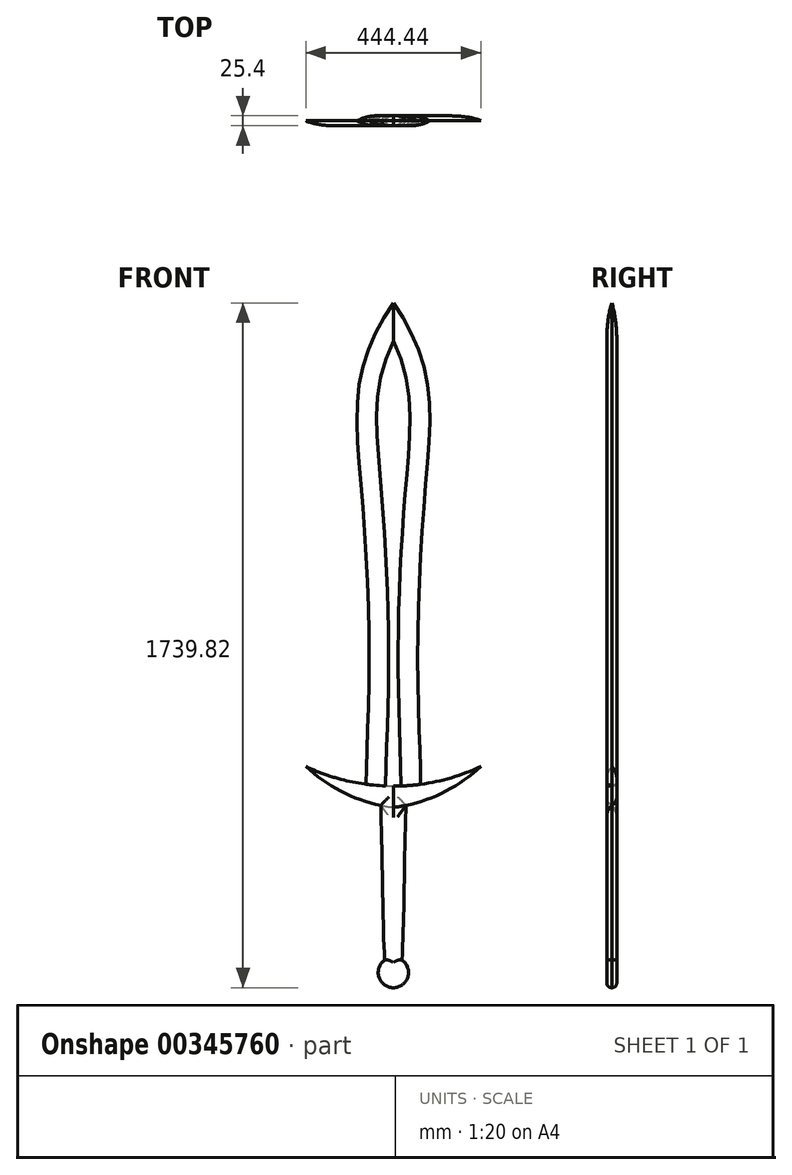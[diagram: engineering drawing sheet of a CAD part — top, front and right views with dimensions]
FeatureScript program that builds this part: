
annotation { "Feature Type Name" : "Feature", "Feature Type Description" : "" }
export const myFeature = defineFeature(function(context is Context, id is Id, definition is map)
    precondition{}
    {
        {
            var Q0;
            Q0=qCreatedBy(makeId("Front.planeOp"),FACE);
            var sketch = newSketch(context, id + "F0", { "sketchPlane" : qUnion([Q0])});
            skLineSegment(sketch, "E0", {"start": v(0, 836.26) * mm, "end": v(0, -840.14) * mm});
            skFitSpline(sketch, "E1", {"points": [v(0, 836.26) * mm, v(-85.7, 634.86) * mm, v(-80.11, 351.26) * mm, v(-61.73, -84.8) * mm, v(-69.32, -386.69) * mm], "startDerivative": vector(-583.16, -808.43) * mm, "endDerivative": vector(-5.13, -843.12) * mm});
            skArc(sketch, "E2", {"start": v(-222.22, -341.63) * mm, "mid": v(-113.84, -378.72) * mm, "end": v(0, -391.38) * mm});
            skArc(sketch, "E3", {"start": v(-222.22, -341.63) * mm, "mid": v(-119.4, -411.33) * mm, "end": v(0, -445.58) * mm});
            skFitSpline(sketch, "E4", {"points": [v(-31.83, -440.37) * mm, v(-29.25, -549) * mm, v(-26.9, -681.75) * mm, v(-21.72, -841.97) * mm], "startDerivative": vector(2.38, -327.28) * mm, "endDerivative": vector(22.91, -400.96) * mm});
            skFitSpline(sketch, "E5.MirrorCS", {"points": [v(0, 836.26) * mm, v(85.7, 634.86) * mm, v(80.11, 351.26) * mm, v(61.73, -84.8) * mm, v(69.32, -386.69) * mm], "startDerivative": vector(583.16, -808.43) * mm, "endDerivative": vector(5.13, -843.12) * mm});
            skArc(sketch, "E6.MirrorCS", {"start": v(222.22, -341.63) * mm, "mid": v(113.84, -378.72) * mm, "end": v(0, -391.38) * mm});
            skArc(sketch, "E7.MirrorCS", {"start": v(222.22, -341.63) * mm, "mid": v(119.4, -411.33) * mm, "end": v(0, -445.58) * mm});
            skFitSpline(sketch, "E8.MirrorCS", {"points": [v(31.83, -440.37) * mm, v(29.25, -549) * mm, v(26.9, -681.75) * mm, v(21.72, -841.97) * mm], "startDerivative": vector(-2.38, -327.28) * mm, "endDerivative": vector(-22.91, -400.96) * mm});
            skCircle(sketch, "E9", {"center": v(0, -865.08) * mm, "radius": 38.48 * mm});
            skSolve(sketch);
        }
        {
            var Q0;
            {var subQ0=sQuery(id+"F0.wireOp",EDGE,"E1");Q0=makeQuery(id+"F0.imprint","IMPRINT",FACE,{"disambiguationData":[TD([[makeQuery(id+"F0.imprint","IMPRINT",EDGE,{"derivedFrom":subQ0}),1.0]])]});}
            var Q1;
            {var subQ0=sQuery(id+"F0.wireOp",EDGE,"E5.MirrorCS");Q1=makeQuery(id+"F0.imprint","IMPRINT",FACE,{"disambiguationData":[TD([[makeQuery(id+"F0.imprint","IMPRINT",EDGE,{"derivedFrom":subQ0}),-1.0]])]});}
            var Q2;
            {var subQ0=sQuery(id+"F0.wireOp",EDGE,"E2");var subQ1=makeQuery(id+"F0.imprint","INTERSECT",VERTEX,{"derivedFrom":[sQuery(id+"F0.wireOp",EDGE,"E1"),subQ0]});Q2=makeQuery(id+"F0.imprint","IMPRINT",FACE,{"disambiguationData":[TD([[makeQuery(id+"F0.imprint","IMPRINT",EDGE,{"disambiguationData":[TD([[subQ1,1.0]])],"derivedFrom":subQ0}),-1.0]])]});}
            var Q3;
            {var subQ1=sQuery(id+"F0.wireOp",EDGE,"E6.MirrorCS");var subQ7=makeQuery(id+"F0.imprint","INTERSECT",VERTEX,{"derivedFrom":[sQuery(id+"F0.wireOp",EDGE,"E5.MirrorCS"),subQ1]});Q3=makeQuery(id+"F0.imprint","IMPRINT",FACE,{"disambiguationData":[TD([[makeQuery(id+"F0.imprint","IMPRINT",EDGE,{"disambiguationData":[TD([[subQ7,1.0]])],"derivedFrom":subQ1}),1.0]])]});}
            var Q4;
            {var subQ0=sQuery(id+"F0.wireOp",EDGE,"E7.MirrorCS");var subQ5=sQuery(id+"F0.wireOp",EDGE,"E8.MirrorCS");var subQ6=makeQuery(id+"F0.imprint","INTERSECT",VERTEX,{"derivedFrom":[subQ0,subQ5]});Q4=makeQuery(id+"F0.imprint","IMPRINT",FACE,{"disambiguationData":[TD([[makeQuery(id+"F0.imprint","IMPRINT",EDGE,{"disambiguationData":[TD([[subQ6,-1.0]])],"derivedFrom":subQ5}),-1.0]])]});}
            var Q5;
            {var subQ0=sQuery(id+"F0.wireOp",EDGE,"E3");var subQ5=sQuery(id+"F0.wireOp",EDGE,"E4");var subQ6=makeQuery(id+"F0.imprint","INTERSECT",VERTEX,{"derivedFrom":[subQ0,subQ5]});Q5=makeQuery(id+"F0.imprint","IMPRINT",FACE,{"disambiguationData":[TD([[makeQuery(id+"F0.imprint","IMPRINT",EDGE,{"disambiguationData":[TD([[subQ6,-1.0]])],"derivedFrom":subQ5}),1.0]])]});}
            var Q6;
            {var subQ0=sQuery(id+"F0.wireOp",EDGE,"E9");var subQ1=makeQuery(id+"F0.imprint","INTERSECT",VERTEX,{"derivedFrom":[sQuery(id+"F0.wireOp",EDGE,"E8.MirrorCS"),subQ0]});Q6=makeQuery(id+"F0.imprint","IMPRINT",FACE,{"disambiguationData":[TD([[makeQuery(id+"F0.imprint","IMPRINT",EDGE,{"disambiguationData":[TD([[subQ1,-1.0]])],"derivedFrom":subQ0}),1.0]])]});}
            extrude(context, id + "F1", {"entities" : qUnion([Q0, Q1, Q2, Q3, Q4, Q5, Q6]), "depth" : 12.7 * mm});
        }
        {
            var Q0;
            Q0=makeQuery(id+"F1.opExtrude","CAP_EDGE",EDGE,{"disambiguationData":[OSD([sQuery(id+"F0.wireOp",EDGE,"E1")])],"isStart":false});
            var Q1;
            Q1=makeQuery(id+"F1.opExtrude","CAP_EDGE",EDGE,{"disambiguationData":[OSD([sQuery(id+"F0.wireOp",EDGE,"E5.MirrorCS")])],"isStart":false});
            fillet(context, id + "F2", {"entities" : qUnion([Q0, Q1]), "radius" : 104.25 * mm, "tangentPropagation" : true, "allowEdgeOverflow" : false});
        }
        {
            var Q0;
            Q0=makeQuery(id+"F1.opExtrude","CAP_EDGE",EDGE,{"disambiguationData":[OSD([sQuery(id+"F0.wireOp",EDGE,"E4")])],"isStart":false});
            var Q1;
            Q1=makeQuery(id+"F1.opExtrude","CAP_EDGE",EDGE,{"disambiguationData":[OSD([sQuery(id+"F0.wireOp",EDGE,"E8.MirrorCS")])],"isStart":false});
            fillet(context, id + "F3", {"entities" : qUnion([Q0, Q1]), "radius" : 23.3 * mm, "tangentPropagation" : true, "allowEdgeOverflow" : false});
        }
        {
            var Q0;
            Q0=makeQuery(id+"F1.opExtrude","CAP_EDGE",EDGE,{"disambiguationData":[OSD([sQuery(id+"F0.wireOp",EDGE,"E9")])],"isStart":false});
            fillet(context, id + "F4", {"entities" : qUnion([Q0]), "radius" : 12.26 * mm, "tangentPropagation" : true, "allowEdgeOverflow" : false});
        }
        {
            var Q0;
            Q0=makeQuery(id+"F1.opExtrude","CAP_EDGE",EDGE,{"disambiguationData":[OSD([sQuery(id+"F0.wireOp",EDGE,"E3")])],"isStart":false});
            var Q1;
            Q1=makeQuery(id+"F1.opExtrude","CAP_EDGE",EDGE,{"disambiguationData":[OSD([sQuery(id+"F0.wireOp",EDGE,"E7.MirrorCS")])],"isStart":false});
            fillet(context, id + "F5", {"entities" : qUnion([Q0, Q1]), "radius" : 30.66 * mm, "tangentPropagation" : true, "allowEdgeOverflow" : false});
        }
        {
            var Q0;
            Q0=makeQuery(id+"F1.opExtrude","CAP_FACE",FACE,{"disambiguationData":[OSD([sQuery(id+"F0.wireOp",EDGE,"E1"),sQuery(id+"F0.wireOp",EDGE,"E2"),sQuery(id+"F0.wireOp",EDGE,"E3"),sQuery(id+"F0.wireOp",EDGE,"E4"),sQuery(id+"F0.wireOp",EDGE,"E5.MirrorCS"),sQuery(id+"F0.wireOp",EDGE,"E6.MirrorCS"),sQuery(id+"F0.wireOp",EDGE,"E7.MirrorCS"),sQuery(id+"F0.wireOp",EDGE,"E8.MirrorCS"),sQuery(id+"F0.wireOp",EDGE,"E9")])],"isStart":true});
            var sketch = newSketch(context, id + "F6", { "sketchPlane" : qUnion([Q0])});
            skLineSegment(sketch, "E10", {"start": v(0, 0) * mm, "end": v(0, 120.77) * mm});
            skSolve(sketch);
        }
        {
            var Q0;
            Q0=makeQuery(id+"F1.opExtrude","SWEPT_BODY",BODY,{"disambiguationData":[OSD([sQuery(id+"F0.wireOp",EDGE,"E1"),sQuery(id+"F0.wireOp",EDGE,"E2"),sQuery(id+"F0.wireOp",EDGE,"E3"),sQuery(id+"F0.wireOp",EDGE,"E4"),sQuery(id+"F0.wireOp",EDGE,"E5.MirrorCS"),sQuery(id+"F0.wireOp",EDGE,"E6.MirrorCS"),sQuery(id+"F0.wireOp",EDGE,"E7.MirrorCS"),sQuery(id+"F0.wireOp",EDGE,"E8.MirrorCS"),sQuery(id+"F0.wireOp",EDGE,"E9")])]});
            var Q1;
            Q1=sQuery(id+"F6.wireOp",EDGE,"E10");
            var Q2;
            Q2=qCreatedBy(makeId("Origin.pointOp"),VERTEX);
            transform(context, id + "F7", {"entities" : qUnion([Q0]), "transformType" : TransformType.ROTATION, "transformAxis" : qUnion([Q1]), "angle" : 180 * degree, "makeCopy" : true});
        }
    });
